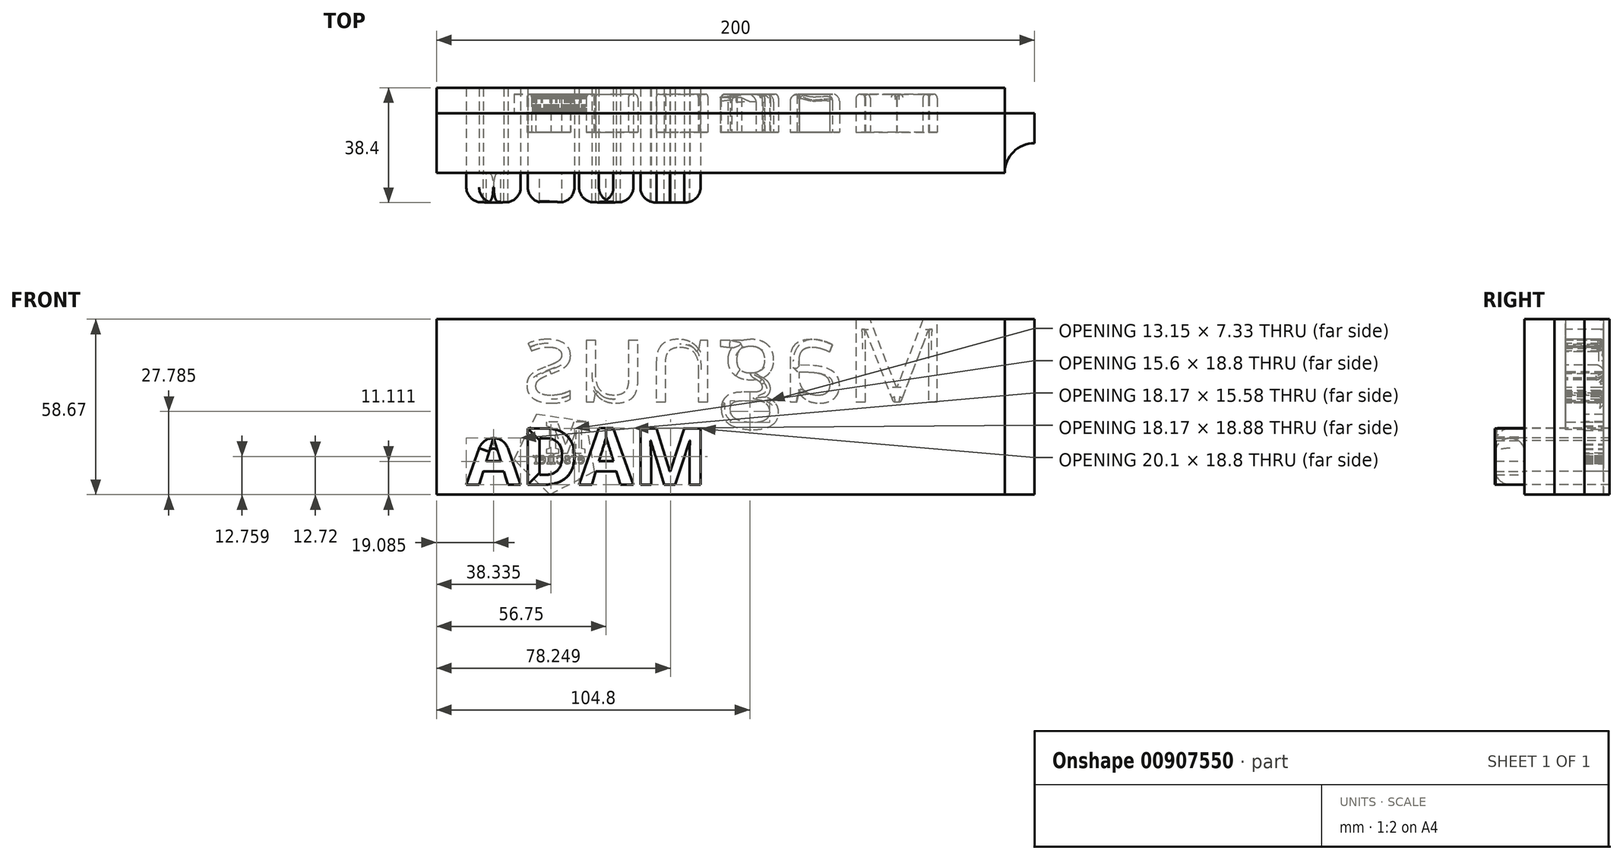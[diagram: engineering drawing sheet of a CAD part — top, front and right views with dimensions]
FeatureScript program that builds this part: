
annotation { "Feature Type Name" : "Feature", "Feature Type Description" : "" }
export const myFeature = defineFeature(function(context is Context, id is Id, definition is map)
    precondition{}
    {
        {
            var Q0;
            Q0=qCreatedBy(makeId("Top.planeOp"),FACE);
            var sketch = newSketch(context, id + "F0", { "sketchPlane" : qUnion([Q0])});
            skLineSegment(sketch, "E0.bottom", {"start": v(-130.3, -9.02) * mm, "end": v(69.7, -9.02) * mm});
            skLineSegment(sketch, "E0.top", {"start": v(-130.3, -29.02) * mm, "end": v(69.7, -29.02) * mm});
            skLineSegment(sketch, "E0.left", {"start": v(-130.3, -9.02) * mm, "end": v(-130.3, -29.02) * mm});
            skLineSegment(sketch, "E0.right", {"start": v(69.7, -9.02) * mm, "end": v(69.7, -29.02) * mm});
            skSolve(sketch);
        }
        {
            var Q0;
            Q0=qSketchRegion(id+"F0",true);
            extrude(context, id + "F1", {"entities" : qUnion([Q0]), "depth" : 58.67 * mm, "offsetDistance" : 25.4 * mm});
        }
        {
            var Q0;
            Q0=makeQuery(id+"F1.opExtrude","CAP_FACE",FACE,{"disambiguationData":[OSD([sQuery(id+"F0.wireOp",EDGE,"E0.bottom"),sQuery(id+"F0.wireOp",EDGE,"E0.top"),sQuery(id+"F0.wireOp",EDGE,"E0.left"),sQuery(id+"F0.wireOp",EDGE,"E0.right")])],"isStart":false});
            var sketch = newSketch(context, id + "F2", { "sketchPlane" : qUnion([Q0])});
            skCircle(sketch, "E1", {"center": v(69.7, -29.02) * mm, "radius": 9.98 * mm});
            skSolve(sketch);
        }
        {
            var Q0;
            Q0=qSketchRegion(id+"F2",true);
            extrude(context, id + "F3", {"entities" : qUnion([Q0]), "operationType" : NewBodyOperationType.REMOVE, "oppositeDirection" : true, "depth" : 70.87 * mm, "offsetDistance" : 25.4 * mm});
        }
        {
            var Q0;
            Q0=makeQuery(id+"F1.opExtrude","SWEPT_FACE",FACE,{"disambiguationData":[OSD([sQuery(id+"F0.wireOp",EDGE,"E0.top")])]});
            var sketch = newSketch(context, id + "F4", { "sketchPlane" : qUnion([Q0])});
            skText(sketch, "E2", { "text": "ADAM", "fontName": "NotoSans-Bold.ttf"});
            const initialGuessF4  = {"E2": [-0.1203, 0.00332, 1, 0, 0.01896]};
            skSetInitialGuess(sketch, initialGuessF4);
            skSolve(sketch);
        }
        {
            var Q0;
            Q0=qSketchRegion(id+"F4",true);
            extrude(context, id + "F5", {"entities" : qUnion([Q0]), "operationType" : NewBodyOperationType.ADD, "depth" : 9.9 * mm, "offsetDistance" : 25.4 * mm});
        }
        {
            var Q0;
            Q0=makeQuery(id+"F5.opExtrude","CAP_EDGE",EDGE,{"disambiguationData":[OSD([sQuery(id+"F4.wireOp",EDGE,"E2.sketch_text.stroke-4")])],"isStart":false});
            fillet(context, id + "F6", {"entities" : qUnion([Q0]), "radius" : 5.08 * mm, "tangentPropagation" : true, "allowEdgeOverflow" : false});
        }
        {
            var Q0;
            Q0=makeQuery(id+"F5.opExtrude","CAP_EDGE",EDGE,{"disambiguationData":[OSD([sQuery(id+"F4.wireOp",EDGE,"E2.sketch_text.stroke-6")])],"isStart":false});
            fillet(context, id + "F7", {"entities" : qUnion([Q0]), "radius" : 5.08 * mm, "tangentPropagation" : true, "allowEdgeOverflow" : false});
        }
        {
            var Q0;
            Q0=makeQuery(id+"F5.opExtrude","CAP_EDGE",EDGE,{"disambiguationData":[OSD([sQuery(id+"F4.wireOp",EDGE,"E2.sketch_text.stroke-15")])],"isStart":false});
            var Q1;
            Q1=makeQuery(id+"F5.opExtrude","CAP_EDGE",EDGE,{"disambiguationData":[OSD([sQuery(id+"F4.wireOp",EDGE,"E2.sketch_text.stroke-12")])],"isStart":false});
            var Q2;
            Q2=makeQuery(id+"F5.opExtrude","CAP_EDGE",EDGE,{"disambiguationData":[OSD([sQuery(id+"F4.wireOp",EDGE,"E2.sketch_text.stroke-28")])],"isStart":false});
            var Q3;
            Q3=makeQuery(id+"F5.opExtrude","CAP_EDGE",EDGE,{"disambiguationData":[OSD([sQuery(id+"F4.wireOp",EDGE,"E2.sketch_text.stroke-30")])],"isStart":false});
            var Q4;
            Q4=makeQuery(id+"F5.opExtrude","CAP_EDGE",EDGE,{"disambiguationData":[OSD([sQuery(id+"F4.wireOp",EDGE,"E2.sketch_text.stroke-41")])],"isStart":false});
            var Q5;
            Q5=makeQuery(id+"F5.opExtrude","CAP_EDGE",EDGE,{"disambiguationData":[OSD([sQuery(id+"F4.wireOp",EDGE,"E2.sketch_text.stroke-47")])],"isStart":false});
            fillet(context, id + "F8", {"entities" : qUnion([Q0, Q1, Q2, Q3, Q4, Q5]), "radius" : 5.08 * mm, "tangentPropagation" : true, "allowEdgeOverflow" : false});
        }
        {
            var Q0;
            Q0=makeQuery(id+"F1.opExtrude","SWEPT_FACE",FACE,{"disambiguationData":[OSD([sQuery(id+"F0.wireOp",EDGE,"E0.bottom")])]});
            var sketch = newSketch(context, id + "F9", { "sketchPlane" : qUnion([Q0])});
            skText(sketch, "E3", { "text": "Magnus", "fontName": "OpenSans-Regular.ttf"});
            const initialGuessF9  = {"E3": [-0.04094, 0.03098, 1, 0, 0.0277]};
            skSetInitialGuess(sketch, initialGuessF9);
            skSolve(sketch);
        }
        {
            var Q0;
            Q0 = qSketchRegion(id + "F9", true);
            var Q1;
            Q1 = qBodyType(qCreatedBy(id + "FaRMMIdU3jUZNCC_1" ,EDGE), BodyType.WIRE);
            extrude(context, id + "F10", {"entities" : qUnion([Q0]), "surfaceEntities" : qUnion([Q1]), "depth" : 12.7 * mm, "offsetDistance" : 25.4 * mm, "symmetric" : true});
        }
        {
            var Q0;
            Q0=makeQuery(id+"F10.opExtrude","CAP_EDGE",EDGE,{"disambiguationData":[OSD([sQuery(id+"F9.wireOp",EDGE,"E3.sketch_text.stroke-11")])],"isStart":false});
            fillet(context, id + "F11", {"entities" : qUnion([Q0]), "radius" : 1.52 * mm, "tangentPropagation" : true, "allowEdgeOverflow" : false});
        }
        {
            var Q0;
            Q0=makeQuery(id+"F10.opExtrude","CAP_EDGE",EDGE,{"disambiguationData":[OSD([sQuery(id+"F9.wireOp",EDGE,"E3.sketch_text.stroke-5")])],"isStart":false});
            fillet(context, id + "F12", {"entities" : qUnion([Q0]), "radius" : 1.27 * mm, "tangentPropagation" : true, "allowEdgeOverflow" : false});
        }
        {
            var Q0;
            Q0=makeQuery(id+"F10.opExtrude","CAP_EDGE",EDGE,{"disambiguationData":[OSD([sQuery(id+"F9.wireOp",EDGE,"E3.sketch_text.stroke-7")])],"isStart":false});
            fillet(context, id + "F13", {"entities" : qUnion([Q0]), "radius" : 1.27 * mm, "allowEdgeOverflow" : false});
        }
        {
            var Q0;
            Q0=makeQuery(id+"F10.opExtrude","CAP_EDGE",EDGE,{"disambiguationData":[OSD([sQuery(id+"F9.wireOp",EDGE,"E3.sketch_text.stroke-9")])],"isStart":false});
            var Q1;
            {var subQ0=sQuery(id+"F9.wireOp",EDGE,"E3.sketch_text.stroke-7");Q1=makeQuery(id+"F13.opFillet","BLEND_EDGE",EDGE,{"blendedFrom":[makeQuery(id+"F10.opExtrude","CAP_EDGE",EDGE,{"disambiguationData":[OSD([subQ0])],"isStart":false}),makeQuery(id+"F10.opExtrude","SWEPT_FACE",FACE,{"disambiguationData":[OSD([subQ0])]})],"blendedInto":[makeQuery(id+"F10.opExtrude","SWEPT_FACE",FACE,{"disambiguationData":[OSD([subQ0])]})]});}
            fillet(context, id + "F14", {"entities" : qUnion([Q0, Q1]), "radius" : 1.27 * mm, "allowEdgeOverflow" : false});
        }
        {
            var Q0;
            Q0=makeQuery(id+"F10.opExtrude","CAP_EDGE",EDGE,{"disambiguationData":[OSD([sQuery(id+"F9.wireOp",EDGE,"E3.sketch_text.stroke-17")])],"isStart":false});
            fillet(context, id + "F15", {"entities" : qUnion([Q0]), "radius" : 1.78 * mm, "tangentPropagation" : true, "allowEdgeOverflow" : false});
        }
        {
            var Q0;
            Q0=makeQuery(id+"F10.opExtrude","CAP_EDGE",EDGE,{"disambiguationData":[OSD([sQuery(id+"F9.wireOp",EDGE,"E3.sketch_text.stroke-18")])],"isStart":false});
            var Q1;
            {var subQ0=sQuery(id+"F9.wireOp",EDGE,"E3.sketch_text.stroke-35");Q1=makeQuery(id+"F18.opFillet","BLEND_EDGE",EDGE,{"blendedFrom":[makeQuery(id+"F10.opExtrude","CAP_EDGE",EDGE,{"disambiguationData":[OSD([subQ0])],"isStart":false}),makeQuery(id+"F17.opFillet","SPLIT",FACE,{"disambiguationData":[OD(0.0)],"derivedFrom":makeQuery(id+"F10.opExtrude","CAP_FACE",FACE,{"disambiguationData":[OSD([sQuery(id+"F9.wireOp",EDGE,"E3.sketch_text.stroke-18"),sQuery(id+"F9.wireOp",EDGE,"E3.sketch_text.stroke-19"),sQuery(id+"F9.wireOp",EDGE,"E3.sketch_text.stroke-20"),sQuery(id+"F9.wireOp",EDGE,"E3.sketch_text.stroke-21"),sQuery(id+"F9.wireOp",EDGE,"E3.sketch_text.stroke-22"),sQuery(id+"F9.wireOp",EDGE,"E3.sketch_text.stroke-23"),sQuery(id+"F9.wireOp",EDGE,"E3.sketch_text.stroke-24"),sQuery(id+"F9.wireOp",EDGE,"E3.sketch_text.stroke-25"),sQuery(id+"F9.wireOp",EDGE,"E3.sketch_text.stroke-26"),sQuery(id+"F9.wireOp",EDGE,"E3.sketch_text.stroke-27"),sQuery(id+"F9.wireOp",EDGE,"E3.sketch_text.stroke-28"),sQuery(id+"F9.wireOp",EDGE,"E3.sketch_text.stroke-29"),sQuery(id+"F9.wireOp",EDGE,"E3.sketch_text.stroke-30"),sQuery(id+"F9.wireOp",EDGE,"E3.sketch_text.stroke-31"),sQuery(id+"F9.wireOp",EDGE,"E3.sketch_text.stroke-32"),sQuery(id+"F9.wireOp",EDGE,"E3.sketch_text.stroke-33"),sQuery(id+"F9.wireOp",EDGE,"E3.sketch_text.stroke-34"),subQ0,sQuery(id+"F9.wireOp",EDGE,"E3.sketch_text.stroke-36"),sQuery(id+"F9.wireOp",EDGE,"E3.sketch_text.stroke-37"),sQuery(id+"F9.wireOp",EDGE,"E3.sketch_text.stroke-38"),sQuery(id+"F9.wireOp",EDGE,"E3.sketch_text.stroke-39"),sQuery(id+"F9.wireOp",EDGE,"E3.sketch_text.stroke-40"),sQuery(id+"F9.wireOp",EDGE,"E3.sketch_text.stroke-41"),sQuery(id+"F9.wireOp",EDGE,"E3.sketch_text.stroke-42"),sQuery(id+"F9.wireOp",EDGE,"E3.sketch_text.stroke-43"),sQuery(id+"F9.wireOp",EDGE,"E3.sketch_text.stroke-44")])],"isStart":false})})],"blendedInto":[makeQuery(id+"F17.opFillet","SPLIT",FACE,{"disambiguationData":[OD(0.0)],"derivedFrom":makeQuery(id+"F10.opExtrude","CAP_FACE",FACE,{"disambiguationData":[OSD([sQuery(id+"F9.wireOp",EDGE,"E3.sketch_text.stroke-18"),sQuery(id+"F9.wireOp",EDGE,"E3.sketch_text.stroke-19"),sQuery(id+"F9.wireOp",EDGE,"E3.sketch_text.stroke-20"),sQuery(id+"F9.wireOp",EDGE,"E3.sketch_text.stroke-21"),sQuery(id+"F9.wireOp",EDGE,"E3.sketch_text.stroke-22"),sQuery(id+"F9.wireOp",EDGE,"E3.sketch_text.stroke-23"),sQuery(id+"F9.wireOp",EDGE,"E3.sketch_text.stroke-24"),sQuery(id+"F9.wireOp",EDGE,"E3.sketch_text.stroke-25"),sQuery(id+"F9.wireOp",EDGE,"E3.sketch_text.stroke-26"),sQuery(id+"F9.wireOp",EDGE,"E3.sketch_text.stroke-27"),sQuery(id+"F9.wireOp",EDGE,"E3.sketch_text.stroke-28"),sQuery(id+"F9.wireOp",EDGE,"E3.sketch_text.stroke-29"),sQuery(id+"F9.wireOp",EDGE,"E3.sketch_text.stroke-30"),sQuery(id+"F9.wireOp",EDGE,"E3.sketch_text.stroke-31"),sQuery(id+"F9.wireOp",EDGE,"E3.sketch_text.stroke-32"),sQuery(id+"F9.wireOp",EDGE,"E3.sketch_text.stroke-33"),sQuery(id+"F9.wireOp",EDGE,"E3.sketch_text.stroke-34"),subQ0,sQuery(id+"F9.wireOp",EDGE,"E3.sketch_text.stroke-36"),sQuery(id+"F9.wireOp",EDGE,"E3.sketch_text.stroke-37"),sQuery(id+"F9.wireOp",EDGE,"E3.sketch_text.stroke-38"),sQuery(id+"F9.wireOp",EDGE,"E3.sketch_text.stroke-39"),sQuery(id+"F9.wireOp",EDGE,"E3.sketch_text.stroke-40"),sQuery(id+"F9.wireOp",EDGE,"E3.sketch_text.stroke-41"),sQuery(id+"F9.wireOp",EDGE,"E3.sketch_text.stroke-42"),sQuery(id+"F9.wireOp",EDGE,"E3.sketch_text.stroke-43"),sQuery(id+"F9.wireOp",EDGE,"E3.sketch_text.stroke-44")])],"isStart":false})})]});}
            fillet(context, id + "F16", {"entities" : qUnion([Q0, Q1]), "radius" : 0.25 * mm, "tangentPropagation" : true, "allowEdgeOverflow" : false});
        }
        {
            var Q0;
            Q0=makeQuery(id+"F10.opExtrude","CAP_EDGE",EDGE,{"disambiguationData":[OSD([sQuery(id+"F9.wireOp",EDGE,"E3.sketch_text.stroke-22")])],"isStart":false});
            var Q1;
            Q1=makeQuery(id+"F10.opExtrude","CAP_EDGE",EDGE,{"disambiguationData":[OSD([sQuery(id+"F9.wireOp",EDGE,"E3.sketch_text.stroke-23")])],"isStart":false});
            var Q2;
            Q2=makeQuery(id+"F10.opExtrude","CAP_EDGE",EDGE,{"disambiguationData":[OSD([sQuery(id+"F9.wireOp",EDGE,"E3.sketch_text.stroke-25")])],"isStart":false});
            var Q3;
            Q3=makeQuery(id+"F10.opExtrude","CAP_EDGE",EDGE,{"disambiguationData":[OSD([sQuery(id+"F9.wireOp",EDGE,"E3.sketch_text.stroke-24")])],"isStart":false});
            var Q4;
            Q4=makeQuery(id+"F10.opExtrude","CAP_EDGE",EDGE,{"disambiguationData":[OSD([sQuery(id+"F9.wireOp",EDGE,"E3.sketch_text.stroke-20")])],"isStart":false});
            var Q5;
            Q5=makeQuery(id+"F10.opExtrude","CAP_EDGE",EDGE,{"disambiguationData":[OSD([sQuery(id+"F9.wireOp",EDGE,"E3.sketch_text.stroke-21")])],"isStart":false});
            fillet(context, id + "F17", {"entities" : qUnion([Q0, Q1, Q2, Q3, Q4, Q5]), "radius" : 2.3 * mm, "allowEdgeOverflow" : false});
        }
        {
            var Q0;
            Q0=makeQuery(id+"F10.opExtrude","CAP_EDGE",EDGE,{"disambiguationData":[OSD([sQuery(id+"F9.wireOp",EDGE,"E3.sketch_text.stroke-35")])],"isStart":false});
            var Q1;
            Q1=makeQuery(id+"F10.opExtrude","CAP_EDGE",EDGE,{"disambiguationData":[OSD([sQuery(id+"F9.wireOp",EDGE,"E3.sketch_text.stroke-32")])],"isStart":false});
            var Q2;
            Q2=makeQuery(id+"F10.opExtrude","CAP_EDGE",EDGE,{"disambiguationData":[OSD([sQuery(id+"F9.wireOp",EDGE,"E3.sketch_text.stroke-34")])],"isStart":false});
            var Q3;
            Q3=makeQuery(id+"F10.opExtrude","CAP_EDGE",EDGE,{"disambiguationData":[OSD([sQuery(id+"F9.wireOp",EDGE,"E3.sketch_text.stroke-33")])],"isStart":false});
            var Q4;
            Q4=makeQuery(id+"F10.opExtrude","CAP_EDGE",EDGE,{"disambiguationData":[OSD([sQuery(id+"F9.wireOp",EDGE,"E3.sketch_text.stroke-31")])],"isStart":false});
            fillet(context, id + "F18", {"entities" : qUnion([Q0, Q1, Q2, Q3, Q4]), "radius" : 2.54 * mm, "tangentPropagation" : true, "allowEdgeOverflow" : false});
        }
        {
            var Q0;
            Q0=makeQuery(id+"F10.opExtrude","CAP_EDGE",EDGE,{"disambiguationData":[OSD([sQuery(id+"F9.wireOp",EDGE,"E3.sketch_text.stroke-71")])],"isStart":false});
            var Q1;
            Q1=makeQuery(id+"F10.opExtrude","CAP_EDGE",EDGE,{"disambiguationData":[OSD([sQuery(id+"F9.wireOp",EDGE,"E3.sketch_text.stroke-72")])],"isStart":false});
            var Q2;
            Q2=makeQuery(id+"F10.opExtrude","CAP_EDGE",EDGE,{"disambiguationData":[OSD([sQuery(id+"F9.wireOp",EDGE,"E3.sketch_text.stroke-68")])],"isStart":false});
            var Q3;
            Q3=makeQuery(id+"F10.opExtrude","CAP_EDGE",EDGE,{"disambiguationData":[OSD([sQuery(id+"F9.wireOp",EDGE,"E3.sketch_text.stroke-70")])],"isStart":false});
            var Q4;
            Q4=makeQuery(id+"F10.opExtrude","CAP_EDGE",EDGE,{"disambiguationData":[OSD([sQuery(id+"F9.wireOp",EDGE,"E3.sketch_text.stroke-69")])],"isStart":false});
            fillet(context, id + "F19", {"entities" : qUnion([Q0, Q1, Q2, Q3, Q4]), "radius" : 2.54 * mm, "tangentPropagation" : true, "allowEdgeOverflow" : false});
        }
        {
            var Q0;
            Q0=makeQuery(id+"F10.opExtrude","CAP_EDGE",EDGE,{"disambiguationData":[OSD([sQuery(id+"F9.wireOp",EDGE,"E3.sketch_text.stroke-66")])],"isStart":false});
            var Q1;
            Q1=makeQuery(id+"F10.opExtrude","CAP_EDGE",EDGE,{"disambiguationData":[OSD([sQuery(id+"F9.wireOp",EDGE,"E3.sketch_text.stroke-64")])],"isStart":false});
            var Q2;
            Q2=makeQuery(id+"F10.opExtrude","CAP_EDGE",EDGE,{"disambiguationData":[OSD([sQuery(id+"F9.wireOp",EDGE,"E3.sketch_text.stroke-65")])],"isStart":false});
            var Q3;
            Q3=makeQuery(id+"F10.opExtrude","CAP_EDGE",EDGE,{"disambiguationData":[OSD([sQuery(id+"F9.wireOp",EDGE,"E3.sketch_text.stroke-63")])],"isStart":false});
            var Q4;
            Q4=makeQuery(id+"F10.opExtrude","CAP_EDGE",EDGE,{"disambiguationData":[OSD([sQuery(id+"F9.wireOp",EDGE,"E3.sketch_text.stroke-61")])],"isStart":false});
            var Q5;
            Q5=makeQuery(id+"F10.opExtrude","CAP_EDGE",EDGE,{"disambiguationData":[OSD([sQuery(id+"F9.wireOp",EDGE,"E3.sketch_text.stroke-59")])],"isStart":false});
            var Q6;
            Q6=makeQuery(id+"F10.opExtrude","CAP_EDGE",EDGE,{"disambiguationData":[OSD([sQuery(id+"F9.wireOp",EDGE,"E3.sketch_text.stroke-58")])],"isStart":false});
            fillet(context, id + "F20", {"entities" : qUnion([Q0, Q1, Q2, Q3, Q4, Q5, Q6]), "radius" : 1.27 * mm, "allowEdgeOverflow" : false});
        }
        {
            var Q0;
            Q0=makeQuery(id+"F10.opExtrude","CAP_EDGE",EDGE,{"disambiguationData":[OSD([sQuery(id+"F9.wireOp",EDGE,"E3.sketch_text.stroke-54")])],"isStart":false});
            var Q1;
            Q1=makeQuery(id+"F10.opExtrude","CAP_EDGE",EDGE,{"disambiguationData":[OSD([sQuery(id+"F9.wireOp",EDGE,"E3.sketch_text.stroke-56")])],"isStart":false});
            var Q2;
            Q2=makeQuery(id+"F10.opExtrude","CAP_EDGE",EDGE,{"disambiguationData":[OSD([sQuery(id+"F9.wireOp",EDGE,"E3.sketch_text.stroke-55")])],"isStart":false});
            fillet(context, id + "F21", {"entities" : qUnion([Q0, Q1, Q2]), "radius" : 1.02 * mm, "tangentPropagation" : true, "allowEdgeOverflow" : false});
        }
        {
            var Q0;
            Q0=makeQuery(id+"F10.opExtrude","CAP_EDGE",EDGE,{"disambiguationData":[OSD([sQuery(id+"F9.wireOp",EDGE,"E3.sketch_text.stroke-50")])],"isStart":false});
            var Q1;
            Q1=makeQuery(id+"F10.opExtrude","CAP_EDGE",EDGE,{"disambiguationData":[OSD([sQuery(id+"F9.wireOp",EDGE,"E3.sketch_text.stroke-48")])],"isStart":false});
            var Q2;
            Q2=makeQuery(id+"F10.opExtrude","CAP_EDGE",EDGE,{"disambiguationData":[OSD([sQuery(id+"F9.wireOp",EDGE,"E3.sketch_text.stroke-49")])],"isStart":false});
            fillet(context, id + "F22", {"entities" : qUnion([Q0, Q1, Q2]), "radius" : 2.54 * mm, "tangentPropagation" : true, "allowEdgeOverflow" : false});
        }
        {
            var Q0;
            Q0=makeQuery(id+"F19.opFillet","BLEND_EDGE",EDGE,{"blendedFrom":[makeQuery(id+"F10.opExtrude","CAP_EDGE",EDGE,{"disambiguationData":[OSD([sQuery(id+"F9.wireOp",EDGE,"E3.sketch_text.stroke-71")])],"isStart":false}),makeQuery(id+"F10.opExtrude","SWEPT_FACE",FACE,{"disambiguationData":[OSD([sQuery(id+"F9.wireOp",EDGE,"E3.sketch_text.stroke-46")])]})],"blendedInto":[makeQuery(id+"F10.opExtrude","SWEPT_FACE",FACE,{"disambiguationData":[OSD([sQuery(id+"F9.wireOp",EDGE,"E3.sketch_text.stroke-46")])]})]});
            fillet(context, id + "F23", {"entities" : qUnion([Q0]), "radius" : 1.27 * mm, "tangentPropagation" : true, "allowEdgeOverflow" : false});
        }
        {
            var Q0;
            Q0=makeQuery(id+"F10.opExtrude","CAP_EDGE",EDGE,{"disambiguationData":[OSD([sQuery(id+"F9.wireOp",EDGE,"E3.sketch_text.stroke-19")])],"isStart":false});
            fillet(context, id + "F24", {"entities" : qUnion([Q0]), "radius" : 1.27 * mm, "tangentPropagation" : true, "allowEdgeOverflow" : false});
        }
        {
            var Q0;
            Q0=makeQuery(id+"F10.opExtrude","CAP_EDGE",EDGE,{"disambiguationData":[OSD([sQuery(id+"F9.wireOp",EDGE,"E3.sketch_text.stroke-26")])],"isStart":false});
            fillet(context, id + "F25", {"entities" : qUnion([Q0]), "radius" : 1.27 * mm, "tangentPropagation" : true, "allowEdgeOverflow" : false});
        }
        {
            var Q0;
            Q0=makeQuery(id+"F10.opExtrude","CAP_EDGE",EDGE,{"disambiguationData":[OSD([sQuery(id+"F9.wireOp",EDGE,"E3.sketch_text.stroke-96")])],"isStart":false});
            fillet(context, id + "F26", {"entities" : qUnion([Q0]), "radius" : 0.76 * mm, "tangentPropagation" : true, "allowEdgeOverflow" : false});
        }
        {
            var Q0;
            Q0=makeQuery(id+"F10.opExtrude","CAP_EDGE",EDGE,{"disambiguationData":[OSD([sQuery(id+"F9.wireOp",EDGE,"E3.sketch_text.stroke-103")])],"isStart":false});
            var Q1;
            Q1=makeQuery(id+"F10.opExtrude","CAP_EDGE",EDGE,{"disambiguationData":[OSD([sQuery(id+"F9.wireOp",EDGE,"E3.sketch_text.stroke-104")])],"isStart":false});
            fillet(context, id + "F27", {"entities" : qUnion([Q0, Q1]), "radius" : 1.02 * mm, "tangentPropagation" : true, "allowEdgeOverflow" : false});
        }
        {
            var Q0;
            Q0=makeQuery(id+"F10.opExtrude","CAP_EDGE",EDGE,{"disambiguationData":[OSD([sQuery(id+"F9.wireOp",EDGE,"E3.sketch_text.stroke-99")])],"isStart":false});
            fillet(context, id + "F28", {"entities" : qUnion([Q0]), "radius" : 1.02 * mm, "tangentPropagation" : true, "allowEdgeOverflow" : false});
        }
        {
            var Q0;
            Q0=makeQuery(id+"F10.opExtrude","CAP_EDGE",EDGE,{"disambiguationData":[OSD([sQuery(id+"F9.wireOp",EDGE,"E3.sketch_text.stroke-117")])],"isStart":false});
            var Q1;
            Q1=makeQuery(id+"F10.opExtrude","CAP_EDGE",EDGE,{"disambiguationData":[OSD([sQuery(id+"F9.wireOp",EDGE,"E3.sketch_text.stroke-118")])],"isStart":false});
            var Q2;
            Q2=makeQuery(id+"F10.opExtrude","CAP_EDGE",EDGE,{"disambiguationData":[OSD([sQuery(id+"F9.wireOp",EDGE,"E3.sketch_text.stroke-121")])],"isStart":false});
            var Q3;
            Q3=makeQuery(id+"F10.opExtrude","CAP_EDGE",EDGE,{"disambiguationData":[OSD([sQuery(id+"F9.wireOp",EDGE,"E3.sketch_text.stroke-120")])],"isStart":false});
            var Q4;
            Q4=makeQuery(id+"F10.opExtrude","CAP_EDGE",EDGE,{"disambiguationData":[OSD([sQuery(id+"F9.wireOp",EDGE,"E3.sketch_text.stroke-119")])],"isStart":false});
            fillet(context, id + "F29", {"entities" : qUnion([Q0, Q1, Q2, Q3, Q4]), "radius" : 1.27 * mm, "tangentPropagation" : true, "allowEdgeOverflow" : false});
        }
        {
            var Q0;
            Q0=makeQuery(id+"F10.opExtrude","CAP_EDGE",EDGE,{"disambiguationData":[OSD([sQuery(id+"F9.wireOp",EDGE,"E3.sketch_text.stroke-113")])],"isStart":false});
            fillet(context, id + "F30", {"entities" : qUnion([Q0]), "radius" : 1.27 * mm, "tangentPropagation" : true, "allowEdgeOverflow" : false});
        }
        {
            var Q0;
            Q0=makeQuery(id+"F10.opExtrude","CAP_EDGE",EDGE,{"disambiguationData":[OSD([sQuery(id+"F9.wireOp",EDGE,"E3.sketch_text.stroke-116")])],"isStart":false});
            fillet(context, id + "F31", {"entities" : qUnion([Q0]), "radius" : 1.02 * mm, "tangentPropagation" : true, "allowEdgeOverflow" : false});
        }
        {
            var Q0;
            Q0=makeQuery(id+"F10.opExtrude","CAP_EDGE",EDGE,{"disambiguationData":[OSD([sQuery(id+"F9.wireOp",EDGE,"E3.sketch_text.stroke-115")])],"isStart":false});
            fillet(context, id + "F32", {"entities" : qUnion([Q0]), "radius" : 0.76 * mm, "tangentPropagation" : true, "allowEdgeOverflow" : false});
        }
        {
            var Q0;
            Q0=makeQuery(id+"F10.opExtrude","CAP_EDGE",EDGE,{"disambiguationData":[OSD([sQuery(id+"F9.wireOp",EDGE,"E3.sketch_text.stroke-125")])],"isStart":false});
            var Q1;
            Q1=makeQuery(id+"F10.opExtrude","CAP_EDGE",EDGE,{"disambiguationData":[OSD([sQuery(id+"F9.wireOp",EDGE,"E3.sketch_text.stroke-124")])],"isStart":false});
            fillet(context, id + "F33", {"entities" : qUnion([Q0, Q1]), "radius" : 1.27 * mm, "tangentPropagation" : true, "allowEdgeOverflow" : false});
        }
        {
            var Q0;
            Q0=makeQuery(id+"F10.opExtrude","CAP_EDGE",EDGE,{"disambiguationData":[OSD([sQuery(id+"F9.wireOp",EDGE,"E3.sketch_text.stroke-128")])],"isStart":false});
            var Q1;
            Q1=makeQuery(id+"F10.opExtrude","CAP_EDGE",EDGE,{"disambiguationData":[OSD([sQuery(id+"F9.wireOp",EDGE,"E3.sketch_text.stroke-127")])],"isStart":false});
            var Q2;
            Q2=makeQuery(id+"F10.opExtrude","CAP_EDGE",EDGE,{"disambiguationData":[OSD([sQuery(id+"F9.wireOp",EDGE,"E3.sketch_text.stroke-136")])],"isStart":false});
            fillet(context, id + "F34", {"entities" : qUnion([Q0, Q1, Q2]), "radius" : 1.27 * mm, "tangentPropagation" : true, "allowEdgeOverflow" : false});
        }
        {
            var Q0;
            Q0=makeQuery(id+"F10.opExtrude","CAP_EDGE",EDGE,{"disambiguationData":[OSD([sQuery(id+"F9.wireOp",EDGE,"E3.sketch_text.stroke-16")])],"isStart":false});
            var Q1;
            Q1=makeQuery(id+"F10.opExtrude","CAP_EDGE",EDGE,{"disambiguationData":[OSD([sQuery(id+"F9.wireOp",EDGE,"E3.sketch_text.stroke-0")])],"isStart":false});
            var Q2;
            Q2=makeQuery(id+"F10.opExtrude","CAP_EDGE",EDGE,{"disambiguationData":[OSD([sQuery(id+"F9.wireOp",EDGE,"E3.sketch_text.stroke-3")])],"isStart":false});
            var Q3;
            Q3=makeQuery(id+"F10.opExtrude","CAP_EDGE",EDGE,{"disambiguationData":[OSD([sQuery(id+"F9.wireOp",EDGE,"E3.sketch_text.stroke-13")])],"isStart":false});
            fillet(context, id + "F35", {"entities" : qUnion([Q0, Q1, Q2, Q3]), "radius" : 1.02 * mm, "tangentPropagation" : true, "allowEdgeOverflow" : false});
        }
        {
            var Q0;
            Q0=makeQuery(id+"F10.opExtrude","CAP_EDGE",EDGE,{"disambiguationData":[OSD([sQuery(id+"F9.wireOp",EDGE,"E3.sketch_text.stroke-90")])],"isStart":false});
            var Q1;
            Q1=makeQuery(id+"F10.opExtrude","CAP_EDGE",EDGE,{"disambiguationData":[OSD([sQuery(id+"F9.wireOp",EDGE,"E3.sketch_text.stroke-89")])],"isStart":false});
            var Q2;
            Q2=makeQuery(id+"F10.opExtrude","CAP_EDGE",EDGE,{"disambiguationData":[OSD([sQuery(id+"F9.wireOp",EDGE,"E3.sketch_text.stroke-94")])],"isStart":false});
            var Q3;
            Q3=makeQuery(id+"F10.opExtrude","CAP_EDGE",EDGE,{"disambiguationData":[OSD([sQuery(id+"F9.wireOp",EDGE,"E3.sketch_text.stroke-93")])],"isStart":false});
            fillet(context, id + "F36", {"entities" : qUnion([Q0, Q1, Q2, Q3]), "radius" : 1.02 * mm, "tangentPropagation" : true, "allowEdgeOverflow" : false});
        }
        {
            var Q0;
            Q0=makeQuery(id+"F10.opExtrude","CAP_EDGE",EDGE,{"disambiguationData":[OSD([sQuery(id+"F9.wireOp",EDGE,"E3.sketch_text.stroke-111")])],"isStart":false});
            var Q1;
            Q1=makeQuery(id+"F10.opExtrude","CAP_EDGE",EDGE,{"disambiguationData":[OSD([sQuery(id+"F9.wireOp",EDGE,"E3.sketch_text.stroke-106")])],"isStart":false});
            fillet(context, id + "F37", {"entities" : qUnion([Q0, Q1]), "radius" : 1.27 * mm, "tangentPropagation" : true, "allowEdgeOverflow" : false});
        }
        {
            var Q0;
            Q0=makeQuery(id+"F10.opExtrude","CAP_EDGE",EDGE,{"disambiguationData":[OSD([sQuery(id+"F9.wireOp",EDGE,"E3.sketch_text.stroke-98")])],"isStart":false});
            fillet(context, id + "F38", {"entities" : qUnion([Q0]), "radius" : 0.76 * mm, "tangentPropagation" : true, "allowEdgeOverflow" : false});
        }
        {
            var Q0;
            Q0=makeQuery(id+"F9.imprint","IMPRINT",FACE,{"disambiguationData":[TD([[makeQuery(id+"F9.imprint","IMPRINT",EDGE,{"derivedFrom":sQuery(id+"F9.wireOp",EDGE,"E3.sketch_text.stroke-0")}),1.0]])]});
            var sketch = newSketch(context, id + "F39", { "sketchPlane" : qUnion([Q0])});
            skCircle(sketch, "E4.cCircle", {"center": v(90.27, 14.16) * mm, "radius": 14.31 * mm, "construction": true});
            skLineSegment(sketch, "E4.0", {"start": v(92.4, 0) * mm, "end": v(77.46, 7.76) * mm});
            skLineSegment(sketch, "E4.1", {"start": v(77.46, 7.76) * mm, "end": v(80.23, 24.36) * mm});
            skLineSegment(sketch, "E4.2", {"start": v(80.23, 24.36) * mm, "end": v(96.87, 26.86) * mm});
            skLineSegment(sketch, "E4.3", {"start": v(96.87, 26.86) * mm, "end": v(104.4, 11.8) * mm});
            skLineSegment(sketch, "E4.4", {"start": v(104.4, 11.8) * mm, "end": v(92.4, 0) * mm});
            skSolve(sketch);
        }
        {
            var Q0;
            Q0=makeQuery(id+"F39.imprint","IMPRINT",FACE,{"disambiguationData":[TD([[makeQuery(id+"F39.imprint","IMPRINT",EDGE,{"derivedFrom":sQuery(id+"F39.wireOp",EDGE,"E4.0")}),-1.0]])]});
            var sketch = newSketch(context, id + "F40", { "sketchPlane" : qUnion([Q0])});
            skSolve(sketch);
        }
        {
            var Q0;
            Q0=makeQuery(id+"F40.imprint","IMPRINT",FACE,{"disambiguationData":[TD([[makeQuery(id+"F40.imprint","IMPRINT",EDGE,{"derivedFrom":makeQuery(id+"F39.imprint","IMPRINT",EDGE,{"derivedFrom":sQuery(id+"F39.wireOp",EDGE,"E4.0")})}),-1.0]])]});
            extrude(context, id + "F41", {"entities" : qUnion([Q0]), "operationType" : NewBodyOperationType.ADD, "depth" : 6.35 * mm, "offsetDistance" : 25.4 * mm});
        }
        {
            var Q0;
            Q0=makeQuery(id+"F41.opExtrude","CAP_FACE",FACE,{"disambiguationData":[OSD([sQuery(id+"F39.wireOp",EDGE,"E4.0"),sQuery(id+"F39.wireOp",EDGE,"E4.1"),sQuery(id+"F39.wireOp",EDGE,"E4.2"),sQuery(id+"F39.wireOp",EDGE,"E4.3"),sQuery(id+"F39.wireOp",EDGE,"E4.4")])],"isStart":false});
            var sketch = newSketch(context, id + "F42", { "sketchPlane" : qUnion([Q0])});
            skText(sketch, "E5", { "text": "M", "fontName": "RobotoSlab-Bold.ttf"});
            const initialGuessF42  = {"E5": [0.08023, 0.01388, 1, 0, 0.01047]};
            skSetInitialGuess(sketch, initialGuessF42);
            skSolve(sketch);
        }
        {
            var Q0;
            Q0 = qSketchRegion(id + "F42", true);
            extrude(context, id + "F43", {"entities" : qUnion([Q0]), "operationType" : NewBodyOperationType.REMOVE, "oppositeDirection" : true, "depth" : 6.35 * mm, "offsetDistance" : 25.4 * mm});
        }
        {
            var Q0;
            Q0=makeQuery(id+"F41.opExtrude","CAP_FACE",FACE,{"disambiguationData":[OSD([sQuery(id+"F39.wireOp",EDGE,"E4.0"),sQuery(id+"F39.wireOp",EDGE,"E4.1"),sQuery(id+"F39.wireOp",EDGE,"E4.2"),sQuery(id+"F39.wireOp",EDGE,"E4.3"),sQuery(id+"F39.wireOp",EDGE,"E4.4")])],"isStart":false});
            var sketch = newSketch(context, id + "F44", { "sketchPlane" : qUnion([Q0])});
            skText(sketch, "E6", { "text": "erscher", "fontName": "RobotoSlab-Regular.ttf"});
            skPoint(sketch, "E6.secondSnap0", {"position": v(98.4, 5.9) * mm});
            const initialGuessF44  = {"E6": [0.08063, 0.01037, 1, 0, 0.00352]};
            skSetInitialGuess(sketch, initialGuessF44);
            skSolve(sketch);
        }
        {
            var Q0;
            Q0 = qSketchRegion(id + "F44", true);
            extrude(context, id + "F45", {"entities" : qUnion([Q0]), "operationType" : NewBodyOperationType.REMOVE, "oppositeDirection" : true, "depth" : 6.35 * mm, "offsetDistance" : 25.4 * mm});
        }
        {
            var Q0;
            {var subQ0=sQuery(id+"F0.wireOp",EDGE,"E0.left");var subQ2=sQuery(id+"F0.wireOp",EDGE,"E0.top");Q0=makeQuery(id+"F5.boolean.opBoolean","SPLIT",FACE,{"disambiguationData":[TD([makeQuery(id+"F1.opExtrude","SWEPT_FACE",FACE,{"disambiguationData":[OSD([subQ0])]})])],"derivedFrom":makeQuery(id+"F1.opExtrude","SWEPT_FACE",FACE,{"disambiguationData":[OSD([subQ2])]})});}
            var sketch = newSketch(context, id + "F46", { "sketchPlane" : qUnion([Q0])});
            skCircle(sketch, "E7", {"center": v(26.9, 40.42) * mm, "radius": 14.88 * mm});
            skSolve(sketch);
        }
        {
            var Q0;
            Q0 = qSketchRegion(id + "F46", true);
            var Q1;
            Q1=makeQuery(id+"F46.imprint","IMPRINT",FACE,{"disambiguationData":[TD([[makeQuery(id+"F46.imprint","IMPRINT",EDGE,{"derivedFrom":sQuery(id+"F46.wireOp",EDGE,"E7")}),-1.0]])]});
            extrude(context, id + "F47", {"entities" : qUnion([Q0, Q1]), "oppositeDirection" : true, "depth" : 28.5 * mm, "offsetDistance" : 25.4 * mm});
        }
    });
